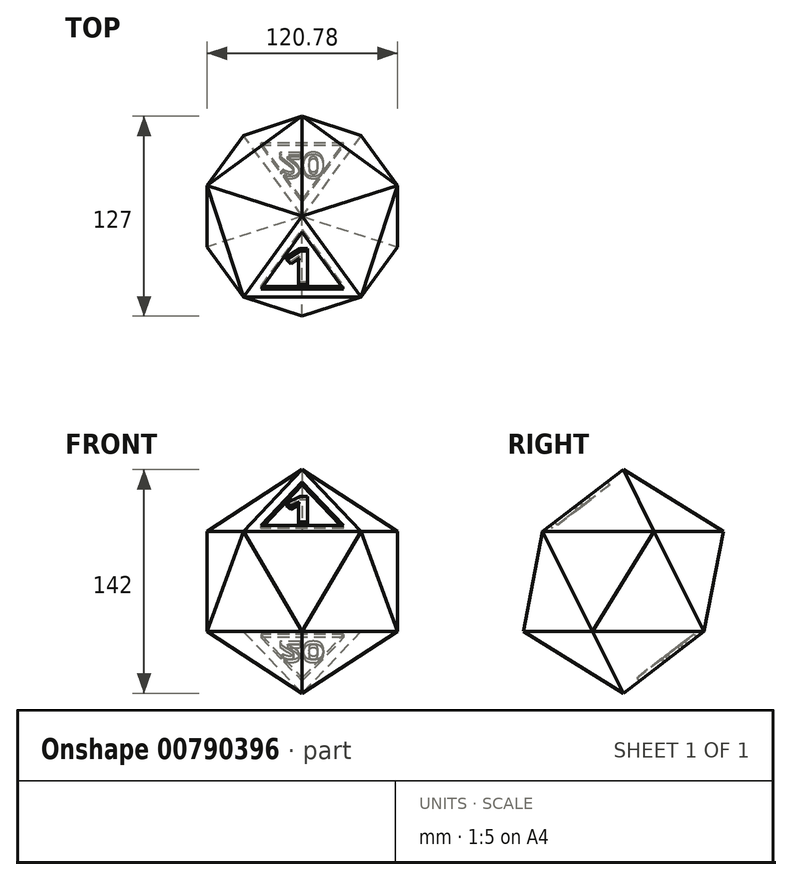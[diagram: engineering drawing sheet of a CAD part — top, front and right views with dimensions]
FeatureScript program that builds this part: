
annotation { "Feature Type Name" : "Feature", "Feature Type Description" : "" }
export const myFeature = defineFeature(function(context is Context, id is Id, definition is map)
    precondition{}
    {
        {
            var Q0;
            Q0=qCreatedBy(makeId("Top.planeOp"),FACE);
            var sketch = newSketch(context, id + "F0", { "sketchPlane" : qUnion([Q0])});
            skCircle(sketch, "E0", {"center": v(37.32, 51.37) * mm, "radius": 74.65 * mm});
            skCircle(sketch, "E1", {"center": v(-37.32, 51.37) * mm, "radius": 74.65 * mm});
            skCircle(sketch, "E2", {"center": v(0, 51.37) * mm, "radius": 64.65 * mm});
            skLineSegment(sketch, "E3", {"start": v(0, 0) * mm, "end": v(39.25, 0) * mm});
            skLineSegment(sketch, "E4", {"start": v(0, 63.5) * mm, "end": v(-63.5, 63.5) * mm});
            skCircle(sketch, "E5", {"center": v(0, 0) * mm, "radius": 63.5 * mm});
            skLineSegment(sketch, "E6", {"start": v(0, 0) * mm, "end": v(0, -63.5) * mm});
            skLineSegment(sketch, "E7", {"start": v(-37.32, 51.37) * mm, "end": v(37.32, 51.37) * mm});
            skLineSegment(sketch, "E8", {"start": v(37.32, 51.37) * mm, "end": v(60.4, -19.62) * mm});
            skLineSegment(sketch, "E9", {"start": v(60.4, -19.62) * mm, "end": v(0, -63.5) * mm});
            skLineSegment(sketch, "E10", {"start": v(0, -63.5) * mm, "end": v(-60.4, -19.62) * mm});
            skLineSegment(sketch, "E11", {"start": v(-60.4, -19.62) * mm, "end": v(-37.32, 51.37) * mm});
            skLineSegment(sketch, "E12", {"start": v(0, 63.5) * mm, "end": v(0, 116.02) * mm});
            skSolve(sketch);
        }
        {
            var Q0;
            Q0=sQuery(id+"F0.wireOp",EDGE,"E4");
            cPlane(context, id + "F1", {"entities" : qUnion([Q0]), "cplaneType" : CPlaneType.LINE_ANGLE, "offset" : 25.4 * mm, "angle" : 180 * degree, "width" : 152.4 * mm, "height" : 152.4 * mm});
        }
        {
            var Q0;
            Q0=qCreatedBy(id+"F1.planeOp",FACE);
            var sketch = newSketch(context, id + "F2", { "sketchPlane" : qUnion([Q0])});
            skLineSegment(sketch, "E13", {"start": v(63.5, 0) * mm, "end": v(0, 0) * mm});
            skLineSegment(sketch, "E14", {"start": v(31.75, 0) * mm, "end": v(63.5, 31.75) * mm});
            skLineSegment(sketch, "E15", {"start": v(31.75, 0) * mm, "end": v(0, -31.75) * mm});
            skLineSegment(sketch, "E16", {"start": v(63.5, 31.75) * mm, "end": v(0, 31.75) * mm});
            skLineSegment(sketch, "E17", {"start": v(0, -31.75) * mm, "end": v(63.5, -31.75) * mm});
            skLineSegment(sketch, "E18", {"start": v(0, 0) * mm, "end": v(0, 31.75) * mm});
            skLineSegment(sketch, "E19", {"start": v(0, 0) * mm, "end": v(0, -31.75) * mm});
            skSolve(sketch);
        }
        {
            var Q0;
            Q0=sQuery(id+"F2.wireOp",EDGE,"E16");
            cPlane(context, id + "F3", {"entities" : qUnion([Q0]), "cplaneType" : CPlaneType.LINE_ANGLE, "offset" : 25.4 * mm, "angle" : 270 * degree, "width" : 152.4 * mm, "height" : 152.4 * mm});
        }
        {
            var Q0;
            Q0=qCreatedBy(id+"F3.planeOp",FACE);
            var sketch = newSketch(context, id + "F4", { "sketchPlane" : qUnion([Q0])});
            skCircle(sketch, "E20.0", {"center": v(0, 0) * mm, "radius": 63.5 * mm});
            skLineSegment(sketch, "E21", {"start": v(-37.32, 51.37) * mm, "end": v(37.32, 51.37) * mm});
            skLineSegment(sketch, "E22", {"start": v(37.32, 51.37) * mm, "end": v(60.4, -19.62) * mm});
            skLineSegment(sketch, "E23", {"start": v(60.4, -19.62) * mm, "end": v(0, -63.5) * mm});
            skLineSegment(sketch, "E24", {"start": v(0, -63.5) * mm, "end": v(-60.4, -19.62) * mm});
            skLineSegment(sketch, "E25", {"start": v(-60.4, -19.62) * mm, "end": v(-37.32, 51.37) * mm});
            skLineSegment(sketch, "E26", {"start": v(0, 51.37) * mm, "end": v(0, 63.5) * mm});
            skLineSegment(sketch, "E27", {"start": v(30.2, -41.56) * mm, "end": v(37.32, -51.37) * mm});
            skLineSegment(sketch, "E28", {"start": v(37.32, -51.37) * mm, "end": v(60.4, -19.62) * mm});
            skLineSegment(sketch, "E29", {"start": v(37.32, -51.37) * mm, "end": v(0, -63.5) * mm});
            skLineSegment(sketch, "E30", {"start": v(-30.2, -41.56) * mm, "end": v(-37.32, -51.37) * mm});
            skLineSegment(sketch, "E31", {"start": v(-37.32, -51.37) * mm, "end": v(0, -63.5) * mm});
            skLineSegment(sketch, "E32", {"start": v(-37.32, -51.37) * mm, "end": v(-60.4, -19.62) * mm});
            skLineSegment(sketch, "E33", {"start": v(-48.86, 15.87) * mm, "end": v(-60.4, 19.62) * mm});
            skLineSegment(sketch, "E34", {"start": v(-60.4, 19.62) * mm, "end": v(-60.4, -19.62) * mm});
            skLineSegment(sketch, "E35", {"start": v(-60.4, 19.62) * mm, "end": v(-37.32, 51.37) * mm});
            skLineSegment(sketch, "E36", {"start": v(-37.32, 51.37) * mm, "end": v(0, 63.5) * mm});
            skLineSegment(sketch, "E37", {"start": v(0, 63.5) * mm, "end": v(37.32, 51.37) * mm});
            skLineSegment(sketch, "E38", {"start": v(60.4, 19.62) * mm, "end": v(37.32, 51.37) * mm});
            skLineSegment(sketch, "E39", {"start": v(60.4, 19.62) * mm, "end": v(60.4, -19.62) * mm});
            skLineSegment(sketch, "E40", {"start": v(48.86, 15.87) * mm, "end": v(60.4, 19.62) * mm});
            skLineSegment(sketch, "E41", {"start": v(0, 0) * mm, "end": v(30.2, -41.56) * mm});
            skLineSegment(sketch, "E42", {"start": v(0, 0) * mm, "end": v(-30.2, -41.56) * mm});
            skLineSegment(sketch, "E43", {"start": v(0, 0) * mm, "end": v(-48.86, 15.87) * mm});
            skLineSegment(sketch, "E44", {"start": v(0, 0) * mm, "end": v(48.86, 15.87) * mm});
            skLineSegment(sketch, "E45", {"start": v(0, 0) * mm, "end": v(0, 51.37) * mm});
            skSolve(sketch);
        }
        {
            var Q0;
            Q0=sQuery(id+"F2.wireOp",EDGE,"E17");
            cPlane(context, id + "F5", {"entities" : qUnion([Q0]), "cplaneType" : CPlaneType.LINE_ANGLE, "offset" : 25.4 * mm, "angle" : 90 * degree, "width" : 152.4 * mm, "height" : 152.4 * mm});
        }
        {
            var Q0;
            Q0=qCreatedBy(id+"F5.planeOp",FACE);
            var sketch = newSketch(context, id + "F6", { "sketchPlane" : qUnion([Q0])});
            skCircle(sketch, "E46.0", {"center": v(0, 0) * mm, "radius": 63.5 * mm});
            skLineSegment(sketch, "E47", {"start": v(-37.32, 51.37) * mm, "end": v(37.32, 51.37) * mm});
            skLineSegment(sketch, "E48", {"start": v(37.32, 51.37) * mm, "end": v(60.4, -19.62) * mm});
            skLineSegment(sketch, "E49", {"start": v(60.4, -19.62) * mm, "end": v(0, -63.5) * mm});
            skLineSegment(sketch, "E50", {"start": v(0, -63.5) * mm, "end": v(-60.4, -19.62) * mm});
            skLineSegment(sketch, "E51", {"start": v(-60.4, -19.62) * mm, "end": v(-37.32, 51.37) * mm});
            skLineSegment(sketch, "E52", {"start": v(0, 51.37) * mm, "end": v(0, 63.5) * mm});
            skLineSegment(sketch, "E53", {"start": v(30.2, -41.56) * mm, "end": v(37.32, -51.37) * mm});
            skLineSegment(sketch, "E54", {"start": v(37.32, -51.37) * mm, "end": v(60.4, -19.62) * mm});
            skLineSegment(sketch, "E55", {"start": v(37.32, -51.37) * mm, "end": v(0, -63.5) * mm});
            skLineSegment(sketch, "E56", {"start": v(-30.2, -41.56) * mm, "end": v(-37.32, -51.37) * mm});
            skLineSegment(sketch, "E57", {"start": v(-37.32, -51.37) * mm, "end": v(0, -63.5) * mm});
            skLineSegment(sketch, "E58", {"start": v(-37.32, -51.37) * mm, "end": v(-60.4, -19.62) * mm});
            skLineSegment(sketch, "E59", {"start": v(-48.86, 15.87) * mm, "end": v(-60.4, 19.62) * mm});
            skLineSegment(sketch, "E60", {"start": v(-60.4, 19.62) * mm, "end": v(-60.4, -19.62) * mm});
            skLineSegment(sketch, "E61", {"start": v(-60.4, 19.62) * mm, "end": v(-37.32, 51.37) * mm});
            skLineSegment(sketch, "E62", {"start": v(-37.32, 51.37) * mm, "end": v(0, 63.5) * mm});
            skLineSegment(sketch, "E63", {"start": v(0, 63.5) * mm, "end": v(37.32, 51.37) * mm});
            skLineSegment(sketch, "E64", {"start": v(60.4, 19.62) * mm, "end": v(37.32, 51.37) * mm});
            skLineSegment(sketch, "E65", {"start": v(60.4, 19.62) * mm, "end": v(60.4, -19.62) * mm});
            skLineSegment(sketch, "E66", {"start": v(48.86, 15.87) * mm, "end": v(60.4, 19.62) * mm});
            skLineSegment(sketch, "E67", {"start": v(0, 0) * mm, "end": v(30.2, -41.56) * mm});
            skLineSegment(sketch, "E68", {"start": v(0, 0) * mm, "end": v(-30.2, -41.56) * mm});
            skLineSegment(sketch, "E69", {"start": v(0, 0) * mm, "end": v(-48.86, 15.88) * mm});
            skLineSegment(sketch, "E70", {"start": v(0, 0) * mm, "end": v(48.86, 15.87) * mm});
            skLineSegment(sketch, "E71", {"start": v(0, 0) * mm, "end": v(0, 51.37) * mm});
            skLineSegment(sketch, "E72.0", {"start": v(-60.4, -19.62) * mm, "end": v(-60.4, 19.62) * mm, "construction": true});
            skLineSegment(sketch, "E73", {"start": v(63.5, 0) * mm, "end": v(74.27, 0) * mm});
            skPoint(sketch, "E73.startSnap0", {"position": v(60.4, 0) * mm});
            skSolve(sketch);
        }
        {
            var Q0;
            Q0=qCreatedBy(makeId("Front.planeOp"),FACE);
            var sketch = newSketch(context, id + "F7", { "sketchPlane" : qUnion([Q0])});
            skLineSegment(sketch, "E74", {"start": v(39.25, 31.75) * mm, "end": v(0, 31.75) * mm});
            skLineSegment(sketch, "E75", {"start": v(39.25, 31.75) * mm, "end": v(0, 71) * mm});
            skLineSegment(sketch, "E76", {"start": v(0, -31.75) * mm, "end": v(39.25, -31.75) * mm});
            skLineSegment(sketch, "E77", {"start": v(39.25, -31.75) * mm, "end": v(0, -71) * mm});
            skLineSegment(sketch, "E78", {"start": v(39.25, -31.75) * mm, "end": v(63.5, -31.75) * mm});
            skLineSegment(sketch, "E79", {"start": v(63.5, -31.75) * mm, "end": v(0, 0) * mm});
            skCircle(sketch, "E80", {"center": v(0, 0) * mm, "radius": 71 * mm});
            skLineSegment(sketch, "E81", {"start": v(0, 0) * mm, "end": v(0, -71) * mm});
            skLineSegment(sketch, "E82", {"start": v(0, 0) * mm, "end": v(0, 71) * mm});
            skLineSegment(sketch, "E83", {"start": v(39.25, 31.75) * mm, "end": v(71, 0) * mm});
            skLineSegment(sketch, "E84", {"start": v(0, 0) * mm, "end": v(39.25, 0) * mm});
            skLineSegment(sketch, "E85", {"start": v(39.25, 0) * mm, "end": v(39.25, 31.75) * mm});
            skSolve(sketch);
        }
        {
            var Q0;
            Q0=qCreatedBy(makeId("Top.planeOp"),FACE);
            var sketch = newSketch(context, id + "F8", { "sketchPlane" : qUnion([Q0])});
            skLineSegment(sketch, "E86", {"start": v(0, 0) * mm, "end": v(71, 0) * mm});
            skCircle(sketch, "E87", {"center": v(0, 0) * mm, "radius": 71 * mm});
            skLineSegment(sketch, "E88", {"start": v(0, 0) * mm, "end": v(67.52, -21.94) * mm});
            skLineSegment(sketch, "E89", {"start": v(0, 0) * mm, "end": v(67.52, 21.94) * mm});
            skLineSegment(sketch, "E90", {"start": v(0, 0) * mm, "end": v(41.73, 57.44) * mm});
            skLineSegment(sketch, "E91", {"start": v(0, 0) * mm, "end": v(0, 71) * mm});
            skLineSegment(sketch, "E92", {"start": v(0, 0) * mm, "end": v(41.73, -57.44) * mm});
            skLineSegment(sketch, "E93", {"start": v(0, 0) * mm, "end": v(0, -71) * mm});
            skLineSegment(sketch, "E94", {"start": v(0, 0) * mm, "end": v(-41.73, -57.44) * mm});
            skLineSegment(sketch, "E95", {"start": v(0, 0) * mm, "end": v(-41.73, 57.44) * mm});
            skLineSegment(sketch, "E96", {"start": v(0, 0) * mm, "end": v(-67.52, 21.94) * mm});
            skLineSegment(sketch, "E97", {"start": v(0, 0) * mm, "end": v(-67.52, -21.94) * mm});
            skSolve(sketch);
        }
        {
            var Q0;
            {var subQ0=sQuery(id+"F7.wireOp",EDGE,"E81");var subQ1=makeQuery(id+"F7.imprint","INTERSECT",VERTEX,{"derivedFrom":[sQuery(id+"F7.wireOp",EDGE,"E76"),subQ0]});Q0=makeQuery(id+"F7.imprint","IMPRINT",FACE,{"disambiguationData":[TD([[makeQuery(id+"F7.imprint","IMPRINT",EDGE,{"disambiguationData":[TD([[subQ1,1.0]])],"derivedFrom":subQ0}),-1.0]])]});}
            var Q1;
            Q1=sQuery(id+"F7.wireOp",EDGE,"E81");
            revolve(context, id + "F9", {"surfaceOperationType" : NewSurfaceOperationType.NEW, "entities" : qUnion([Q0]), "axis" : qUnion([Q1]), "revolveType" : RevolveType.FULL});
        }
        {
            var Q0;
            Q0=sQuery(id+"F6.wireOp",VERTEX,"E53.end");
            var Q1;
            Q1=sQuery(id+"F6.wireOp",VERTEX,"E67.start");
            var Q2;
            Q2=sQuery(id+"F7.wireOp",VERTEX,"E77.end");
            cPlane(context, id + "F10", {"entities" : qUnion([Q0, Q1, Q2]), "cplaneType" : CPlaneType.THREE_POINT, "offset" : 25.4 * mm, "width" : 152.4 * mm, "height" : 152.4 * mm});
        }
        {
            var Q0;
            Q0=qCreatedBy(id+"F10.planeOp",FACE);
            var sketch = newSketch(context, id + "F11", { "sketchPlane" : qUnion([Q0])});
            skLineSegment(sketch, "E98", {"start": v(0, -71) * mm, "end": v(-51.37, -31.75) * mm});
            skLineSegment(sketch, "E99", {"start": v(-51.37, -31.75) * mm, "end": v(-63.5, -31.75) * mm});
            skLineSegment(sketch, "E100", {"start": v(-63.5, -31.75) * mm, "end": v(-63.5, -71) * mm});
            skLineSegment(sketch, "E101", {"start": v(-63.5, -71) * mm, "end": v(0, -71) * mm});
            skSolve(sketch);
        }
        {
            var Q0;
            {var subQ0=sQuery(id+"F11.wireOp",EDGE,"E98");Q0=makeQuery(id+"F11.imprint","IMPRINT",FACE,{"disambiguationData":[TD([[makeQuery(id+"F11.imprint","IMPRINT",EDGE,{"derivedFrom":subQ0}),1.0]])]});}
            var Q1;
            Q1=sQuery(id+"F6.wireOp",VERTEX,"E48.end");
            var Q2;
            Q2=sQuery(id+"F6.wireOp",VERTEX,"E49.end");
            extrude(context, id + "F12", {"entities" : qUnion([Q0]), "operationType" : NewBodyOperationType.REMOVE, "endBound" : BoundingType.UP_TO_VERTEX, "depth" : 25.4 * mm, "endBoundEntityVertex" : qUnion([Q1]), "offsetDistance" : 25.4 * mm, "hasSecondDirection" : true, "secondDirectionBound" : SecondDirectionBoundingType.UP_TO_VERTEX, "secondDirectionOppositeDirection" : true, "secondDirectionDepth" : 25.4 * mm, "secondDirectionBoundEntityVertex" : qUnion([Q2])});
        }
        {
            var Q0;
            Q0=sQuery(id+"F7.wireOp",VERTEX,"E77.end");
            var Q1;
            Q1=sQuery(id+"F6.wireOp",VERTEX,"E67.start");
            var Q2;
            Q2=sQuery(id+"F6.wireOp",VERTEX,"E56.end");
            cPlane(context, id + "F13", {"entities" : qUnion([Q0, Q1, Q2]), "cplaneType" : CPlaneType.THREE_POINT, "offset" : 25.4 * mm, "width" : 152.4 * mm, "height" : 152.4 * mm});
        }
        {
            var Q0;
            Q0=qCreatedBy(id+"F13.planeOp",FACE);
            var sketch = newSketch(context, id + "F14", { "sketchPlane" : qUnion([Q0])});
            skLineSegment(sketch, "E102", {"start": v(0, -71) * mm, "end": v(51.37, -31.75) * mm});
            skLineSegment(sketch, "E103", {"start": v(0, -71) * mm, "end": v(63.5, -71) * mm});
            skLineSegment(sketch, "E104", {"start": v(63.5, -71) * mm, "end": v(63.5, -31.75) * mm});
            skLineSegment(sketch, "E105", {"start": v(63.5, -31.75) * mm, "end": v(51.37, -31.75) * mm});
            skSolve(sketch);
        }
        {
            var Q0;
            {var subQ0=sQuery(id+"F14.wireOp",EDGE,"E102");Q0=makeQuery(id+"F14.imprint","IMPRINT",FACE,{"disambiguationData":[TD([[makeQuery(id+"F14.imprint","IMPRINT",EDGE,{"derivedFrom":subQ0}),-1.0]])]});}
            var Q1;
            Q1=sQuery(id+"F6.wireOp",VERTEX,"E49.end");
            var Q2;
            Q2=sQuery(id+"F6.wireOp",VERTEX,"E50.end");
            extrude(context, id + "F15", {"entities" : qUnion([Q0]), "operationType" : NewBodyOperationType.REMOVE, "endBound" : BoundingType.UP_TO_VERTEX, "oppositeDirection" : true, "depth" : 25.4 * mm, "endBoundEntityVertex" : qUnion([Q1]), "offsetDistance" : 25.4 * mm, "hasSecondDirection" : true, "secondDirectionBound" : SecondDirectionBoundingType.UP_TO_VERTEX, "secondDirectionOppositeDirection" : false, "secondDirectionDepth" : 25.4 * mm, "secondDirectionBoundEntityVertex" : qUnion([Q2])});
        }
        {
            var Q0;
            Q0=sQuery(id+"F6.wireOp",VERTEX,"E67.start");
            var Q1;
            Q1=sQuery(id+"F7.wireOp",VERTEX,"E77.end");
            var Q2;
            Q2=sQuery(id+"F6.wireOp",VERTEX,"E59.end");
            cPlane(context, id + "F16", {"entities" : qUnion([Q0, Q1, Q2]), "cplaneType" : CPlaneType.THREE_POINT, "offset" : 25.4 * mm, "width" : 152.4 * mm, "height" : 152.4 * mm});
        }
        {
            var Q0;
            Q0=qCreatedBy(id+"F16.planeOp",FACE);
            var sketch = newSketch(context, id + "F17", { "sketchPlane" : qUnion([Q0])});
            skLineSegment(sketch, "E106", {"start": v(0, -71) * mm, "end": v(-51.37, -31.75) * mm});
            skLineSegment(sketch, "E107", {"start": v(0, -71) * mm, "end": v(-63.5, -71) * mm});
            skLineSegment(sketch, "E108", {"start": v(-63.5, -71) * mm, "end": v(-63.5, -31.75) * mm});
            skLineSegment(sketch, "E109", {"start": v(-63.5, -31.75) * mm, "end": v(-51.37, -31.75) * mm});
            skSolve(sketch);
        }
        {
            var Q0;
            {var subQ0=sQuery(id+"F17.wireOp",EDGE,"E106");Q0=makeQuery(id+"F17.imprint","IMPRINT",FACE,{"disambiguationData":[TD([[makeQuery(id+"F17.imprint","IMPRINT",EDGE,{"derivedFrom":subQ0}),1.0]])]});}
            var Q1;
            Q1=sQuery(id+"F6.wireOp",VERTEX,"E47.start");
            var Q2;
            Q2=sQuery(id+"F6.wireOp",VERTEX,"E50.end");
            extrude(context, id + "F18", {"entities" : qUnion([Q0]), "operationType" : NewBodyOperationType.REMOVE, "endBound" : BoundingType.UP_TO_VERTEX, "oppositeDirection" : true, "depth" : 25.4 * mm, "endBoundEntityVertex" : qUnion([Q1]), "offsetDistance" : 25.4 * mm, "hasSecondDirection" : true, "secondDirectionBound" : SecondDirectionBoundingType.UP_TO_VERTEX, "secondDirectionOppositeDirection" : false, "secondDirectionDepth" : 25.4 * mm, "secondDirectionBoundEntityVertex" : qUnion([Q2])});
        }
        {
            var Q0;
            Q0=sQuery(id+"F7.wireOp",VERTEX,"E77.end");
            var Q1;
            Q1=sQuery(id+"F6.wireOp",VERTEX,"E67.start");
            var Q2;
            Q2=sQuery(id+"F6.wireOp",VERTEX,"E52.end");
            cPlane(context, id + "F19", {"entities" : qUnion([Q0, Q1, Q2]), "cplaneType" : CPlaneType.THREE_POINT, "offset" : 25.4 * mm, "width" : 152.4 * mm, "height" : 152.4 * mm});
        }
        {
            var Q0;
            Q0=qCreatedBy(id+"F19.planeOp",FACE);
            var sketch = newSketch(context, id + "F20", { "sketchPlane" : qUnion([Q0])});
            skLineSegment(sketch, "E110", {"start": v(0, -71) * mm, "end": v(51.37, -31.75) * mm});
            skLineSegment(sketch, "E111", {"start": v(0, -71) * mm, "end": v(63.5, -71) * mm});
            skLineSegment(sketch, "E112", {"start": v(63.5, -71) * mm, "end": v(63.5, -31.75) * mm});
            skLineSegment(sketch, "E113", {"start": v(63.5, -31.75) * mm, "end": v(51.37, -31.75) * mm});
            skSolve(sketch);
        }
        {
            var Q0;
            {var subQ0=sQuery(id+"F20.wireOp",EDGE,"E110");Q0=makeQuery(id+"F20.imprint","IMPRINT",FACE,{"disambiguationData":[TD([[makeQuery(id+"F20.imprint","IMPRINT",EDGE,{"derivedFrom":subQ0}),-1.0]])]});}
            var Q1;
            Q1=sQuery(id+"F6.wireOp",VERTEX,"E47.start");
            var Q2;
            Q2=sQuery(id+"F6.wireOp",VERTEX,"E47.end");
            extrude(context, id + "F21", {"entities" : qUnion([Q0]), "operationType" : NewBodyOperationType.REMOVE, "endBound" : BoundingType.UP_TO_VERTEX, "oppositeDirection" : true, "depth" : 25.4 * mm, "endBoundEntityVertex" : qUnion([Q1]), "offsetDistance" : 25.4 * mm, "hasSecondDirection" : true, "secondDirectionBound" : SecondDirectionBoundingType.UP_TO_VERTEX, "secondDirectionOppositeDirection" : false, "secondDirectionDepth" : 25.4 * mm, "secondDirectionBoundEntityVertex" : qUnion([Q2])});
        }
        {
            var Q0;
            Q0=sQuery(id+"F6.wireOp",VERTEX,"E64.start");
            var Q1;
            Q1=sQuery(id+"F6.wireOp",VERTEX,"E67.start");
            var Q2;
            Q2=sQuery(id+"F7.wireOp",VERTEX,"E77.end");
            cPlane(context, id + "F22", {"entities" : qUnion([Q0, Q1, Q2]), "cplaneType" : CPlaneType.THREE_POINT, "offset" : 25.4 * mm, "width" : 152.4 * mm, "height" : 152.4 * mm});
        }
        {
            var Q0;
            Q0=qCreatedBy(id+"F22.planeOp",FACE);
            var sketch = newSketch(context, id + "F23", { "sketchPlane" : qUnion([Q0])});
            skLineSegment(sketch, "E114", {"start": v(0, -71) * mm, "end": v(-51.37, -31.75) * mm});
            skLineSegment(sketch, "E115", {"start": v(-51.37, -31.75) * mm, "end": v(-63.5, -31.75) * mm});
            skLineSegment(sketch, "E116", {"start": v(-63.5, -31.75) * mm, "end": v(-63.5, -71) * mm});
            skLineSegment(sketch, "E117", {"start": v(-63.5, -71) * mm, "end": v(0, -71) * mm});
            skSolve(sketch);
        }
        {
            var Q0;
            {var subQ0=sQuery(id+"F23.wireOp",EDGE,"E114");Q0=makeQuery(id+"F23.imprint","IMPRINT",FACE,{"disambiguationData":[TD([[makeQuery(id+"F23.imprint","IMPRINT",EDGE,{"derivedFrom":subQ0}),1.0]])]});}
            var Q1;
            Q1=sQuery(id+"F6.wireOp",VERTEX,"E47.end");
            var Q2;
            Q2=sQuery(id+"F6.wireOp",VERTEX,"E48.end");
            extrude(context, id + "F24", {"entities" : qUnion([Q0]), "operationType" : NewBodyOperationType.REMOVE, "endBound" : BoundingType.UP_TO_VERTEX, "depth" : 25.4 * mm, "endBoundEntityVertex" : qUnion([Q1]), "offsetDistance" : 25.4 * mm, "hasSecondDirection" : true, "secondDirectionBound" : SecondDirectionBoundingType.UP_TO_VERTEX, "secondDirectionOppositeDirection" : true, "secondDirectionDepth" : 25.4 * mm, "secondDirectionBoundEntityVertex" : qUnion([Q2])});
        }
        {
            var Q0;
            Q0=sQuery(id+"F6.wireOp",EDGE,"E49");
            cPoint(context, id + "F25", {"entities" : qUnion([Q0]), "parameter" : 0.5});
        }
        {
            var Q0;
            Q0=qCreatedBy(id+"F25",VERTEX);
            var Q1;
            Q1=sQuery(id+"F6.wireOp",VERTEX,"E53.end");
            var Q2;
            Q2=sQuery(id+"F4.wireOp",VERTEX,"E21.end");
            cPlane(context, id + "F26", {"entities" : qUnion([Q0, Q1, Q2]), "cplaneType" : CPlaneType.THREE_POINT, "offset" : 25.4 * mm, "width" : 152.4 * mm, "height" : 152.4 * mm});
        }
        {
            var Q0;
            Q0=qCreatedBy(id+"F26.planeOp",FACE);
            var sketch = newSketch(context, id + "F27", { "sketchPlane" : qUnion([Q0])});
            skLineSegment(sketch, "E118.bottom", {"start": v(-51.37, -31.75) * mm, "end": v(-71, -31.75) * mm});
            skLineSegment(sketch, "E118.top", {"start": v(-51.37, 31.75) * mm, "end": v(-71, 31.75) * mm});
            skLineSegment(sketch, "E118.left", {"start": v(-51.37, -31.75) * mm, "end": v(-51.37, 31.75) * mm});
            skLineSegment(sketch, "E118.right", {"start": v(-71, -31.75) * mm, "end": v(-71, 31.75) * mm});
            skLineSegment(sketch, "E119", {"start": v(-51.37, -31.75) * mm, "end": v(-63.5, 31.75) * mm});
            skSolve(sketch);
        }
        {
            var Q0;
            Q0=makeQuery(id+"F27.imprint","IMPRINT",FACE,{"disambiguationData":[TD([[makeQuery(id+"F27.imprint","IMPRINT",EDGE,{"derivedFrom":sQuery(id+"F27.wireOp",EDGE,"E118.bottom")}),-1.0]])]});
            var Q1;
            Q1=sQuery(id+"F6.wireOp",VERTEX,"E48.end");
            var Q2;
            Q2=sQuery(id+"F6.wireOp",VERTEX,"E49.end");
            extrude(context, id + "F28", {"entities" : qUnion([Q0]), "operationType" : NewBodyOperationType.REMOVE, "endBound" : BoundingType.THROUGH_ALL, "depth" : 25.4 * mm, "endBoundEntityVertex" : qUnion([Q1]), "offsetDistance" : 25.4 * mm, "hasSecondDirection" : true, "secondDirectionBound" : SecondDirectionBoundingType.THROUGH_ALL, "secondDirectionOppositeDirection" : true, "secondDirectionDepth" : 25.4 * mm, "secondDirectionBoundEntityVertex" : qUnion([Q2])});
        }
        {
            var Q0;
            Q0=sQuery(id+"F4.wireOp",EDGE,"E22");
            cPoint(context, id + "F29", {"entities" : qUnion([Q0]), "parameter" : 0.5});
        }
        {
            var Q0;
            Q0=sQuery(id+"F6.wireOp",VERTEX,"E48.end");
            var Q1;
            Q1=qCreatedBy(id+"F29",VERTEX);
            var Q2;
            Q2=sQuery(id+"F4.wireOp",VERTEX,"E38.start");
            cPlane(context, id + "F30", {"entities" : qUnion([Q0, Q1, Q2]), "cplaneType" : CPlaneType.THREE_POINT, "offset" : 25.4 * mm, "width" : 152.4 * mm, "height" : 152.4 * mm});
        }
        {
            var Q0;
            Q0=qCreatedBy(id+"F30.planeOp",FACE);
            var sketch = newSketch(context, id + "F31", { "sketchPlane" : qUnion([Q0])});
            skLineSegment(sketch, "E120.bottom", {"start": v(51.37, 31.75) * mm, "end": v(71, 31.75) * mm});
            skLineSegment(sketch, "E120.top", {"start": v(51.37, -31.75) * mm, "end": v(71, -31.75) * mm});
            skLineSegment(sketch, "E120.left", {"start": v(51.37, 31.75) * mm, "end": v(51.37, -31.75) * mm});
            skLineSegment(sketch, "E120.right", {"start": v(71, 31.75) * mm, "end": v(71, -31.75) * mm});
            skLineSegment(sketch, "E121", {"start": v(51.37, 31.75) * mm, "end": v(63.5, -31.75) * mm});
            skSolve(sketch);
        }
        {
            var Q0;
            Q0=makeQuery(id+"F58.imprint","IMPRINT",FACE,{"disambiguationData":[TD([[makeQuery(id+"F58.imprint","IMPRINT",EDGE,{"derivedFrom":sQuery(id+"F58.wireOp",EDGE,"E136.bottom")}),-1.0]])]});
            var Q1;
            Q1=makeQuery(id+"F31.imprint","IMPRINT",FACE,{"disambiguationData":[TD([[makeQuery(id+"F31.imprint","IMPRINT",EDGE,{"derivedFrom":sQuery(id+"F31.wireOp",EDGE,"E120.bottom")}),-1.0]])]});
            extrude(context, id + "F32", {"entities" : qUnion([Q0, Q1]), "operationType" : NewBodyOperationType.REMOVE, "endBound" : BoundingType.THROUGH_ALL, "oppositeDirection" : true, "depth" : 25.4 * mm, "offsetDistance" : 25.4 * mm, "hasSecondDirection" : true, "secondDirectionBound" : SecondDirectionBoundingType.THROUGH_ALL, "secondDirectionOppositeDirection" : false, "secondDirectionDepth" : 25.4 * mm});
        }
        {
            var Q0;
            Q0=sQuery(id+"F6.wireOp",VERTEX,"E64.start");
            var Q1;
            Q1=sQuery(id+"F6.wireOp",VERTEX,"E66.start");
            var Q2;
            Q2=sQuery(id+"F4.wireOp",VERTEX,"E22.end");
            cPlane(context, id + "F33", {"entities" : qUnion([Q0, Q1, Q2]), "cplaneType" : CPlaneType.THREE_POINT, "offset" : 25.4 * mm, "width" : 152.4 * mm, "height" : 152.4 * mm});
        }
        {
            var Q0;
            Q0=qCreatedBy(id+"F33.planeOp",FACE);
            var sketch = newSketch(context, id + "F34", { "sketchPlane" : qUnion([Q0])});
            skLineSegment(sketch, "E122.bottom", {"start": v(51.37, -31.75) * mm, "end": v(71, -31.75) * mm});
            skLineSegment(sketch, "E122.top", {"start": v(51.37, 31.75) * mm, "end": v(71, 31.75) * mm});
            skLineSegment(sketch, "E122.left", {"start": v(51.37, -31.75) * mm, "end": v(51.37, 31.75) * mm});
            skLineSegment(sketch, "E122.right", {"start": v(71, -31.75) * mm, "end": v(71, 31.75) * mm});
            skLineSegment(sketch, "E123", {"start": v(51.37, -31.75) * mm, "end": v(63.5, 31.75) * mm});
            skSolve(sketch);
        }
        {
            var Q0;
            Q0=makeQuery(id+"F55.imprint","IMPRINT",FACE,{"disambiguationData":[TD([[makeQuery(id+"F55.imprint","IMPRINT",EDGE,{"derivedFrom":sQuery(id+"F55.wireOp",EDGE,"E134.bottom")}),-1.0]])]});
            var Q1;
            Q1=makeQuery(id+"F34.imprint","IMPRINT",FACE,{"disambiguationData":[TD([[makeQuery(id+"F34.imprint","IMPRINT",EDGE,{"derivedFrom":sQuery(id+"F34.wireOp",EDGE,"E122.bottom")}),1.0]])]});
            extrude(context, id + "F35", {"entities" : qUnion([Q0, Q1]), "operationType" : NewBodyOperationType.REMOVE, "endBound" : BoundingType.THROUGH_ALL, "oppositeDirection" : true, "depth" : 25.4 * mm, "offsetDistance" : 25.4 * mm, "hasSecondDirection" : true, "secondDirectionBound" : SecondDirectionBoundingType.THROUGH_ALL, "secondDirectionOppositeDirection" : false, "secondDirectionDepth" : 25.4 * mm});
        }
        {
            var Q0;
            Q0=sQuery(id+"F4.wireOp",EDGE,"E23");
            cPoint(context, id + "F36", {"entities" : qUnion([Q0]), "parameter" : 0.5});
        }
        {
            var Q0;
            Q0=qCreatedBy(id+"F36",VERTEX);
            var Q1;
            Q1=sQuery(id+"F4.wireOp",VERTEX,"E27.end");
            var Q2;
            Q2=sQuery(id+"F6.wireOp",VERTEX,"E47.end");
            cPlane(context, id + "F37", {"entities" : qUnion([Q0, Q1, Q2]), "cplaneType" : CPlaneType.THREE_POINT, "offset" : 25.4 * mm, "width" : 152.4 * mm, "height" : 152.4 * mm});
        }
        {
            var Q0;
            Q0=qCreatedBy(id+"F37.planeOp",FACE);
            var sketch = newSketch(context, id + "F38", { "sketchPlane" : qUnion([Q0])});
            skLineSegment(sketch, "E124.bottom", {"start": v(51.37, 31.75) * mm, "end": v(71, 31.75) * mm});
            skLineSegment(sketch, "E124.top", {"start": v(51.37, -31.75) * mm, "end": v(71, -31.75) * mm});
            skLineSegment(sketch, "E124.left", {"start": v(51.37, 31.75) * mm, "end": v(51.37, -31.75) * mm});
            skLineSegment(sketch, "E124.right", {"start": v(71, 31.75) * mm, "end": v(71, -31.75) * mm});
            skLineSegment(sketch, "E125", {"start": v(51.37, 31.75) * mm, "end": v(63.5, -31.75) * mm});
            skSolve(sketch);
        }
        {
            var Q0;
            Q0=makeQuery(id+"F38.imprint","IMPRINT",FACE,{"disambiguationData":[TD([[makeQuery(id+"F38.imprint","IMPRINT",EDGE,{"derivedFrom":sQuery(id+"F38.wireOp",EDGE,"E124.bottom")}),-1.0]])]});
            extrude(context, id + "F39", {"entities" : qUnion([Q0]), "operationType" : NewBodyOperationType.REMOVE, "endBound" : BoundingType.THROUGH_ALL, "oppositeDirection" : true, "depth" : 25.4 * mm, "offsetDistance" : 25.4 * mm, "hasSecondDirection" : true, "secondDirectionBound" : SecondDirectionBoundingType.THROUGH_ALL, "secondDirectionOppositeDirection" : false, "secondDirectionDepth" : 25.4 * mm});
        }
        {
            var Q0;
            Q0=sQuery(id+"F6.wireOp",VERTEX,"E52.start");
            var Q1;
            Q1=sQuery(id+"F6.wireOp",VERTEX,"E52.end");
            var Q2;
            Q2=sQuery(id+"F4.wireOp",VERTEX,"E23.end");
            cPlane(context, id + "F40", {"entities" : qUnion([Q0, Q1, Q2]), "cplaneType" : CPlaneType.THREE_POINT, "offset" : 25.4 * mm, "width" : 152.4 * mm, "height" : 152.4 * mm});
        }
        {
            var Q0;
            Q0=qCreatedBy(id+"F40.planeOp",FACE);
            var sketch = newSketch(context, id + "F41", { "sketchPlane" : qUnion([Q0])});
            skLineSegment(sketch, "E126.bottom", {"start": v(-51.37, -31.75) * mm, "end": v(-71, -31.75) * mm});
            skLineSegment(sketch, "E126.top", {"start": v(-51.37, 31.75) * mm, "end": v(-71, 31.75) * mm});
            skLineSegment(sketch, "E126.left", {"start": v(-51.37, -31.75) * mm, "end": v(-51.37, 31.75) * mm});
            skLineSegment(sketch, "E126.right", {"start": v(-71, -31.75) * mm, "end": v(-71, 31.75) * mm});
            skLineSegment(sketch, "E127", {"start": v(-51.37, -31.75) * mm, "end": v(-63.5, 31.75) * mm});
            skSolve(sketch);
        }
        {
            var Q0;
            Q0=makeQuery(id+"F41.imprint","IMPRINT",FACE,{"disambiguationData":[TD([[makeQuery(id+"F41.imprint","IMPRINT",EDGE,{"derivedFrom":sQuery(id+"F41.wireOp",EDGE,"E126.bottom")}),-1.0]])]});
            extrude(context, id + "F42", {"entities" : qUnion([Q0]), "operationType" : NewBodyOperationType.REMOVE, "endBound" : BoundingType.THROUGH_ALL, "oppositeDirection" : true, "depth" : 25.4 * mm, "offsetDistance" : 25.4 * mm, "hasSecondDirection" : true, "secondDirectionBound" : SecondDirectionBoundingType.THROUGH_ALL, "secondDirectionOppositeDirection" : false, "secondDirectionDepth" : 25.4 * mm});
        }
        {
            var Q0;
            Q0=sQuery(id+"F4.wireOp",VERTEX,"E30.end");
            var Q1;
            Q1=sQuery(id+"F4.wireOp",VERTEX,"E30.start");
            var Q2;
            Q2=sQuery(id+"F6.wireOp",VERTEX,"E47.start");
            cPlane(context, id + "F43", {"entities" : qUnion([Q0, Q1, Q2]), "cplaneType" : CPlaneType.THREE_POINT, "offset" : 25.4 * mm, "width" : 152.4 * mm, "height" : 152.4 * mm});
        }
        {
            var Q0;
            Q0=qCreatedBy(id+"F43.planeOp",FACE);
            var sketch = newSketch(context, id + "F44", { "sketchPlane" : qUnion([Q0])});
            skLineSegment(sketch, "E128.bottom", {"start": v(-51.37, 31.75) * mm, "end": v(-71, 31.75) * mm});
            skLineSegment(sketch, "E128.top", {"start": v(-51.37, -31.75) * mm, "end": v(-71, -31.75) * mm});
            skLineSegment(sketch, "E128.left", {"start": v(-51.37, 31.75) * mm, "end": v(-51.37, -31.75) * mm});
            skLineSegment(sketch, "E128.right", {"start": v(-71, 31.75) * mm, "end": v(-71, -31.75) * mm});
            skLineSegment(sketch, "E129", {"start": v(-51.37, 31.75) * mm, "end": v(-63.5, -31.75) * mm});
            skSolve(sketch);
        }
        {
            var Q0;
            Q0=makeQuery(id+"F44.imprint","IMPRINT",FACE,{"disambiguationData":[TD([[makeQuery(id+"F44.imprint","IMPRINT",EDGE,{"derivedFrom":sQuery(id+"F44.wireOp",EDGE,"E128.bottom")}),1.0]])]});
            extrude(context, id + "F45", {"entities" : qUnion([Q0]), "operationType" : NewBodyOperationType.REMOVE, "endBound" : BoundingType.THROUGH_ALL, "oppositeDirection" : true, "depth" : 25.4 * mm, "offsetDistance" : 25.4 * mm, "hasSecondDirection" : true, "secondDirectionBound" : SecondDirectionBoundingType.THROUGH_ALL, "secondDirectionOppositeDirection" : false, "secondDirectionDepth" : 25.4 * mm});
        }
        {
            var Q0;
            Q0=sQuery(id+"F6.wireOp",VERTEX,"E59.start");
            var Q1;
            Q1=sQuery(id+"F6.wireOp",VERTEX,"E59.end");
            var Q2;
            Q2=sQuery(id+"F4.wireOp",VERTEX,"E24.end");
            cPlane(context, id + "F46", {"entities" : qUnion([Q0, Q1, Q2]), "cplaneType" : CPlaneType.THREE_POINT, "offset" : 25.4 * mm, "width" : 152.4 * mm, "height" : 152.4 * mm});
        }
        {
            var Q0;
            Q0=qCreatedBy(id+"F46.planeOp",FACE);
            var sketch = newSketch(context, id + "F47", { "sketchPlane" : qUnion([Q0])});
            skLineSegment(sketch, "E130.bottom", {"start": v(-51.37, -31.75) * mm, "end": v(-71, -31.75) * mm});
            skLineSegment(sketch, "E130.top", {"start": v(-51.37, 31.75) * mm, "end": v(-71, 31.75) * mm});
            skLineSegment(sketch, "E130.left", {"start": v(-51.37, -31.75) * mm, "end": v(-51.37, 31.75) * mm});
            skLineSegment(sketch, "E130.right", {"start": v(-71, -31.75) * mm, "end": v(-71, 31.75) * mm});
            skLineSegment(sketch, "E131", {"start": v(-51.37, -31.75) * mm, "end": v(-63.5, 31.75) * mm});
            skSolve(sketch);
        }
        {
            var Q0;
            Q0=makeQuery(id+"F47.imprint","IMPRINT",FACE,{"disambiguationData":[TD([[makeQuery(id+"F47.imprint","IMPRINT",EDGE,{"derivedFrom":sQuery(id+"F47.wireOp",EDGE,"E130.bottom")}),-1.0]])]});
            extrude(context, id + "F48", {"entities" : qUnion([Q0]), "operationType" : NewBodyOperationType.REMOVE, "endBound" : BoundingType.THROUGH_ALL, "oppositeDirection" : true, "depth" : 25.4 * mm, "offsetDistance" : 25.4 * mm, "hasSecondDirection" : true, "secondDirectionBound" : SecondDirectionBoundingType.THROUGH_ALL, "secondDirectionOppositeDirection" : false, "secondDirectionDepth" : 25.4 * mm});
        }
        {
            var Q0;
            Q0=sQuery(id+"F4.wireOp",EDGE,"E25");
            cPoint(context, id + "F49", {"entities" : qUnion([Q0]), "parameter" : 0.5});
        }
        {
            var Q0;
            Q0=sQuery(id+"F6.wireOp",VERTEX,"E50.end");
            var Q1;
            Q1=qCreatedBy(id+"F49",VERTEX);
            var Q2;
            Q2=sQuery(id+"F4.wireOp",VERTEX,"E33.end");
            cPlane(context, id + "F50", {"entities" : qUnion([Q0, Q1, Q2]), "cplaneType" : CPlaneType.THREE_POINT, "offset" : 25.4 * mm, "width" : 152.4 * mm, "height" : 152.4 * mm});
        }
        {
            var Q0;
            Q0=qCreatedBy(id+"F50.planeOp",FACE);
            var sketch = newSketch(context, id + "F51", { "sketchPlane" : qUnion([Q0])});
            skLineSegment(sketch, "E132.bottom", {"start": v(51.37, 31.75) * mm, "end": v(71, 31.75) * mm});
            skLineSegment(sketch, "E132.top", {"start": v(51.37, -31.75) * mm, "end": v(71, -31.75) * mm});
            skLineSegment(sketch, "E132.left", {"start": v(51.37, 31.75) * mm, "end": v(51.37, -31.75) * mm});
            skLineSegment(sketch, "E132.right", {"start": v(71, 31.75) * mm, "end": v(71, -31.75) * mm});
            skLineSegment(sketch, "E133", {"start": v(51.37, 31.75) * mm, "end": v(63.5, -31.75) * mm});
            skSolve(sketch);
        }
        {
            var Q0;
            Q0=makeQuery(id+"F51.imprint","IMPRINT",FACE,{"disambiguationData":[TD([[makeQuery(id+"F51.imprint","IMPRINT",EDGE,{"derivedFrom":sQuery(id+"F51.wireOp",EDGE,"E132.bottom")}),-1.0]])]});
            extrude(context, id + "F52", {"entities" : qUnion([Q0]), "operationType" : NewBodyOperationType.REMOVE, "endBound" : BoundingType.THROUGH_ALL, "oppositeDirection" : true, "depth" : 25.4 * mm, "offsetDistance" : 25.4 * mm, "hasSecondDirection" : true, "secondDirectionBound" : SecondDirectionBoundingType.THROUGH_ALL, "secondDirectionOppositeDirection" : false, "secondDirectionDepth" : 25.4 * mm});
        }
        {
            var Q0;
            Q0=sQuery(id+"F6.wireOp",EDGE,"E50");
            cPoint(context, id + "F53", {"entities" : qUnion([Q0]), "parameter" : 0.5});
        }
        {
            var Q0;
            Q0=qCreatedBy(id+"F53",VERTEX);
            var Q1;
            Q1=sQuery(id+"F6.wireOp",VERTEX,"E56.end");
            var Q2;
            Q2=sQuery(id+"F4.wireOp",VERTEX,"E21.start");
            cPlane(context, id + "F54", {"entities" : qUnion([Q0, Q1, Q2]), "cplaneType" : CPlaneType.THREE_POINT, "offset" : 25.4 * mm, "width" : 152.4 * mm, "height" : 152.4 * mm});
        }
        {
            var Q0;
            Q0=qCreatedBy(id+"F54.planeOp",FACE);
            var sketch = newSketch(context, id + "F55", { "sketchPlane" : qUnion([Q0])});
            skLineSegment(sketch, "E134.bottom", {"start": v(-51.37, -31.75) * mm, "end": v(-71, -31.75) * mm});
            skLineSegment(sketch, "E134.top", {"start": v(-51.37, 31.75) * mm, "end": v(-71, 31.75) * mm});
            skLineSegment(sketch, "E134.left", {"start": v(-51.37, -31.75) * mm, "end": v(-51.37, 31.75) * mm});
            skLineSegment(sketch, "E134.right", {"start": v(-71, -31.75) * mm, "end": v(-71, 31.75) * mm});
            skLineSegment(sketch, "E135", {"start": v(-51.37, -31.75) * mm, "end": v(-63.5, 31.75) * mm});
            skSolve(sketch);
        }
        {
            var Q0;
            Q0=makeQuery(id+"F55.imprint","IMPRINT",FACE,{"disambiguationData":[TD([[makeQuery(id+"F55.imprint","IMPRINT",EDGE,{"derivedFrom":sQuery(id+"F55.wireOp",EDGE,"E134.bottom")}),-1.0]])]});
            extrude(context, id + "F56", {"entities" : qUnion([Q0]), "operationType" : NewBodyOperationType.REMOVE, "endBound" : BoundingType.THROUGH_ALL, "oppositeDirection" : true, "depth" : 25.4 * mm, "offsetDistance" : 25.4 * mm, "hasSecondDirection" : true, "secondDirectionBound" : SecondDirectionBoundingType.THROUGH_ALL, "secondDirectionOppositeDirection" : false, "secondDirectionDepth" : 25.4 * mm});
        }
        {
            var Q0;
            Q0=sQuery(id+"F6.wireOp",VERTEX,"E49.end");
            var Q1;
            Q1=sQuery(id+"F4.wireOp",VERTEX,"E26.start");
            var Q2;
            Q2=sQuery(id+"F4.wireOp",VERTEX,"E26.end");
            cPlane(context, id + "F57", {"entities" : qUnion([Q0, Q1, Q2]), "cplaneType" : CPlaneType.THREE_POINT, "offset" : 25.4 * mm, "width" : 152.4 * mm, "height" : 152.4 * mm});
        }
        {
            var Q0;
            Q0=qCreatedBy(id+"F57.planeOp",FACE);
            var sketch = newSketch(context, id + "F58", { "sketchPlane" : qUnion([Q0])});
            skLineSegment(sketch, "E136.bottom", {"start": v(51.37, 31.75) * mm, "end": v(71, 31.75) * mm});
            skLineSegment(sketch, "E136.top", {"start": v(51.37, -31.75) * mm, "end": v(71, -31.75) * mm});
            skLineSegment(sketch, "E136.left", {"start": v(51.37, 31.75) * mm, "end": v(51.37, -31.75) * mm});
            skLineSegment(sketch, "E136.right", {"start": v(71, 31.75) * mm, "end": v(71, -31.75) * mm});
            skLineSegment(sketch, "E137", {"start": v(51.37, 31.75) * mm, "end": v(63.5, -31.75) * mm});
            skSolve(sketch);
        }
        {
            var Q0;
            Q0=makeQuery(id+"F58.imprint","IMPRINT",FACE,{"disambiguationData":[TD([[makeQuery(id+"F58.imprint","IMPRINT",EDGE,{"derivedFrom":sQuery(id+"F58.wireOp",EDGE,"E136.bottom")}),-1.0]])]});
            extrude(context, id + "F59", {"entities" : qUnion([Q0]), "operationType" : NewBodyOperationType.REMOVE, "endBound" : BoundingType.THROUGH_ALL, "oppositeDirection" : true, "depth" : 25.4 * mm, "offsetDistance" : 25.4 * mm, "hasSecondDirection" : true, "secondDirectionBound" : SecondDirectionBoundingType.THROUGH_ALL, "secondDirectionOppositeDirection" : false, "secondDirectionDepth" : 25.4 * mm});
        }
        {
            var Q0;
            Q0=sQuery(id+"F4.wireOp",VERTEX,"E41.start");
            var Q1;
            Q1=sQuery(id+"F7.wireOp",VERTEX,"E75.end");
            var Q2;
            Q2=sQuery(id+"F4.wireOp",VERTEX,"E38.start");
            cPlane(context, id + "F60", {"entities" : qUnion([Q0, Q1, Q2]), "cplaneType" : CPlaneType.THREE_POINT, "offset" : 25.4 * mm, "width" : 152.4 * mm, "height" : 152.4 * mm});
        }
        {
            var Q0;
            Q0=qCreatedBy(id+"F60.planeOp",FACE);
            var sketch = newSketch(context, id + "F61", { "sketchPlane" : qUnion([Q0])});
            skLineSegment(sketch, "E138", {"start": v(0, 71) * mm, "end": v(51.37, 31.75) * mm});
            skLineSegment(sketch, "E139", {"start": v(0, 71) * mm, "end": v(63.5, 71) * mm});
            skLineSegment(sketch, "E140", {"start": v(63.5, 71) * mm, "end": v(63.5, 31.75) * mm});
            skLineSegment(sketch, "E141", {"start": v(63.5, 31.75) * mm, "end": v(51.37, 31.75) * mm});
            skSolve(sketch);
        }
        {
            var Q0;
            {var subQ0=sQuery(id+"F61.wireOp",EDGE,"E138");Q0=makeQuery(id+"F61.imprint","IMPRINT",FACE,{"disambiguationData":[TD([[makeQuery(id+"F61.imprint","IMPRINT",EDGE,{"derivedFrom":subQ0}),1.0]])]});}
            var Q1;
            Q1=sQuery(id+"F4.wireOp",VERTEX,"E21.end");
            var Q2;
            Q2=sQuery(id+"F4.wireOp",VERTEX,"E22.end");
            extrude(context, id + "F62", {"entities" : qUnion([Q0]), "operationType" : NewBodyOperationType.REMOVE, "endBound" : BoundingType.UP_TO_VERTEX, "depth" : 25.4 * mm, "endBoundEntityVertex" : qUnion([Q1]), "offsetDistance" : 25.4 * mm, "hasSecondDirection" : true, "secondDirectionBound" : SecondDirectionBoundingType.UP_TO_VERTEX, "secondDirectionOppositeDirection" : true, "secondDirectionDepth" : 25.4 * mm, "secondDirectionBoundEntityVertex" : qUnion([Q2])});
        }
        {
            var Q0;
            Q0=sQuery(id+"F7.wireOp",VERTEX,"E75.end");
            var Q1;
            Q1=sQuery(id+"F4.wireOp",VERTEX,"E41.start");
            var Q2;
            Q2=sQuery(id+"F4.wireOp",VERTEX,"E26.end");
            cPlane(context, id + "F63", {"entities" : qUnion([Q0, Q1, Q2]), "cplaneType" : CPlaneType.THREE_POINT, "offset" : 25.4 * mm, "width" : 152.4 * mm, "height" : 152.4 * mm});
        }
        {
            var Q0;
            Q0=qCreatedBy(id+"F63.planeOp",FACE);
            var sketch = newSketch(context, id + "F64", { "sketchPlane" : qUnion([Q0])});
            skLineSegment(sketch, "E142", {"start": v(0, 71) * mm, "end": v(-51.37, 31.75) * mm});
            skLineSegment(sketch, "E143", {"start": v(0, 71) * mm, "end": v(-63.5, 71) * mm});
            skLineSegment(sketch, "E144", {"start": v(-63.5, 71) * mm, "end": v(-63.5, 31.75) * mm});
            skLineSegment(sketch, "E145", {"start": v(-63.5, 31.75) * mm, "end": v(-51.37, 31.75) * mm});
            skSolve(sketch);
        }
        {
            var Q0;
            Q0=makeQuery(id+"F64.imprint","IMPRINT",FACE,{"disambiguationData":[TD([[makeQuery(id+"F64.imprint","IMPRINT",EDGE,{"derivedFrom":sQuery(id+"F64.wireOp",EDGE,"E142")}),-1.0]])]});
            extrude(context, id + "F65", {"entities" : qUnion([Q0]), "operationType" : NewBodyOperationType.REMOVE, "endBound" : BoundingType.THROUGH_ALL, "oppositeDirection" : true, "depth" : 25.4 * mm, "offsetDistance" : 25.4 * mm, "hasSecondDirection" : true, "secondDirectionBound" : SecondDirectionBoundingType.THROUGH_ALL, "secondDirectionOppositeDirection" : false, "secondDirectionDepth" : 25.4 * mm});
        }
        {
            var Q0;
            Q0=sQuery(id+"F7.wireOp",VERTEX,"E75.end");
            var Q1;
            Q1=sQuery(id+"F4.wireOp",VERTEX,"E41.start");
            var Q2;
            Q2=sQuery(id+"F4.wireOp",VERTEX,"E33.end");
            cPlane(context, id + "F66", {"entities" : qUnion([Q0, Q1, Q2]), "cplaneType" : CPlaneType.THREE_POINT, "offset" : 25.4 * mm, "width" : 152.4 * mm, "height" : 152.4 * mm});
        }
        {
            var Q0;
            Q0=qCreatedBy(id+"F66.planeOp",FACE);
            var sketch = newSketch(context, id + "F67", { "sketchPlane" : qUnion([Q0])});
            skLineSegment(sketch, "E146", {"start": v(0, 71) * mm, "end": v(-51.37, 31.75) * mm});
            skLineSegment(sketch, "E147", {"start": v(0, 71) * mm, "end": v(-63.5, 71) * mm});
            skLineSegment(sketch, "E148", {"start": v(-63.5, 71) * mm, "end": v(-63.5, 31.75) * mm});
            skLineSegment(sketch, "E149", {"start": v(-63.5, 31.75) * mm, "end": v(-51.37, 31.75) * mm});
            skSolve(sketch);
        }
        {
            var Q0;
            {var subQ0=sQuery(id+"F67.wireOp",EDGE,"E146");Q0=makeQuery(id+"F67.imprint","IMPRINT",FACE,{"disambiguationData":[TD([[makeQuery(id+"F67.imprint","IMPRINT",EDGE,{"derivedFrom":subQ0}),-1.0]])]});}
            extrude(context, id + "F68", {"entities" : qUnion([Q0]), "operationType" : NewBodyOperationType.REMOVE, "endBound" : BoundingType.THROUGH_ALL, "oppositeDirection" : true, "depth" : 25.4 * mm, "offsetDistance" : 25.4 * mm, "hasSecondDirection" : true, "secondDirectionBound" : SecondDirectionBoundingType.THROUGH_ALL, "secondDirectionOppositeDirection" : false, "secondDirectionDepth" : 25.4 * mm});
        }
        {
            var Q0;
            Q0=sQuery(id+"F4.wireOp",VERTEX,"E30.end");
            var Q1;
            Q1=sQuery(id+"F4.wireOp",VERTEX,"E41.start");
            var Q2;
            Q2=sQuery(id+"F7.wireOp",VERTEX,"E75.end");
            cPlane(context, id + "F69", {"entities" : qUnion([Q0, Q1, Q2]), "cplaneType" : CPlaneType.THREE_POINT, "offset" : 25.4 * mm, "width" : 152.4 * mm, "height" : 152.4 * mm});
        }
        {
            var Q0;
            Q0=qCreatedBy(id+"F69.planeOp",FACE);
            var sketch = newSketch(context, id + "F70", { "sketchPlane" : qUnion([Q0])});
            skLineSegment(sketch, "E150", {"start": v(0, 71) * mm, "end": v(51.37, 31.75) * mm});
            skLineSegment(sketch, "E151", {"start": v(0, 71) * mm, "end": v(63.5, 71) * mm});
            skLineSegment(sketch, "E152", {"start": v(63.5, 71) * mm, "end": v(63.5, 31.75) * mm});
            skLineSegment(sketch, "E153", {"start": v(63.5, 31.75) * mm, "end": v(51.37, 31.75) * mm});
            skSolve(sketch);
        }
        {
            var Q0;
            Q0=makeQuery(id+"F70.imprint","IMPRINT",FACE,{"disambiguationData":[TD([[makeQuery(id+"F70.imprint","IMPRINT",EDGE,{"derivedFrom":sQuery(id+"F70.wireOp",EDGE,"E150")}),1.0]])]});
            extrude(context, id + "F71", {"entities" : qUnion([Q0]), "operationType" : NewBodyOperationType.REMOVE, "endBound" : BoundingType.THROUGH_ALL, "oppositeDirection" : true, "depth" : 25.4 * mm, "offsetDistance" : 25.4 * mm, "hasSecondDirection" : true, "secondDirectionBound" : SecondDirectionBoundingType.THROUGH_ALL, "secondDirectionOppositeDirection" : false, "secondDirectionDepth" : 25.4 * mm});
        }
        {
            var Q0;
            Q0=sQuery(id+"F4.wireOp",VERTEX,"E27.end");
            var Q1;
            Q1=sQuery(id+"F4.wireOp",VERTEX,"E41.start");
            var Q2;
            Q2=sQuery(id+"F7.wireOp",VERTEX,"E75.end");
            cPlane(context, id + "F72", {"entities" : qUnion([Q0, Q1, Q2]), "cplaneType" : CPlaneType.THREE_POINT, "offset" : 25.4 * mm, "width" : 152.4 * mm, "height" : 152.4 * mm});
        }
        {
            var Q0;
            Q0=qCreatedBy(id+"F72.planeOp",FACE);
            var sketch = newSketch(context, id + "F73", { "sketchPlane" : qUnion([Q0])});
            skLineSegment(sketch, "E154", {"start": v(0, 71) * mm, "end": v(51.37, 31.75) * mm});
            skLineSegment(sketch, "E155", {"start": v(0, 71) * mm, "end": v(63.5, 71) * mm});
            skLineSegment(sketch, "E156", {"start": v(63.5, 71) * mm, "end": v(63.5, 31.75) * mm});
            skLineSegment(sketch, "E157", {"start": v(63.5, 31.75) * mm, "end": v(51.37, 31.75) * mm});
            skSolve(sketch);
        }
        {
            var Q0;
            {var subQ0=sQuery(id+"F73.wireOp",EDGE,"E154");Q0=makeQuery(id+"F73.imprint","IMPRINT",FACE,{"disambiguationData":[TD([[makeQuery(id+"F73.imprint","IMPRINT",EDGE,{"derivedFrom":subQ0}),1.0]])]});}
            extrude(context, id + "F74", {"entities" : qUnion([Q0]), "operationType" : NewBodyOperationType.REMOVE, "endBound" : BoundingType.THROUGH_ALL, "oppositeDirection" : true, "depth" : 25.4 * mm, "offsetDistance" : 25.4 * mm, "hasSecondDirection" : true, "secondDirectionBound" : SecondDirectionBoundingType.THROUGH_ALL, "secondDirectionOppositeDirection" : false, "secondDirectionDepth" : 25.4 * mm});
        }
        {
            var Q0;
            Q0=makeQuery(id+"F65.boolean.opBoolean","COPY",FACE,{"derivedFrom":makeQuery(id+"F65.opExtrude","SWEPT_FACE",FACE,{"disambiguationData":[OSD([sQuery(id+"F64.wireOp",EDGE,"E142")])]})});
            var sketch = newSketch(context, id + "F75", { "sketchPlane" : qUnion([Q0])});
            skText(sketch, "E158", { "text": "1", "fontName": "OpenSans-Bold.ttf"});
            skLineSegment(sketch, "E159", {"start": v(-37.32, -21.55) * mm, "end": v(0, 43.1) * mm});
            skLineSegment(sketch, "E160", {"start": v(0, 43.1) * mm, "end": v(37.32, -21.55) * mm});
            skLineSegment(sketch, "E161", {"start": v(37.32, -21.55) * mm, "end": v(-37.32, -21.55) * mm});
            skLineSegment(sketch, "E162.0", {"start": v(0, 30.4) * mm, "end": v(26.33, -15.2) * mm});
            skLineSegment(sketch, "E162.1", {"start": v(-26.33, -15.2) * mm, "end": v(0, 30.4) * mm});
            skLineSegment(sketch, "E162.2", {"start": v(26.33, -15.2) * mm, "end": v(-26.33, -15.2) * mm});
            const initialGuessF75  = {"E158": [-0.01221, -0.01159, 1, 0, 0.02712]};
            skSetInitialGuess(sketch, initialGuessF75);
            skSolve(sketch);
        }
        {
            var Q0;
            Q0=makeQuery(id+"F75.imprint","IMPRINT",FACE,{"disambiguationData":[TD([[makeQuery(id+"F75.imprint","IMPRINT",EDGE,{"derivedFrom":sQuery(id+"F75.wireOp",EDGE,"E158.sketch_text.stroke-0")}),1.0]])]});
            extrude(context, id + "F76", {"entities" : qUnion([Q0]), "operationType" : NewBodyOperationType.REMOVE, "oppositeDirection" : true, "depth" : 2.54 * mm, "offsetDistance" : 25.4 * mm});
        }
        {
            var Q0;
            Q0=makeQuery(id+"F21.boolean.opBoolean","COPY",FACE,{"derivedFrom":makeQuery(id+"F21.opExtrude","SWEPT_FACE",FACE,{"disambiguationData":[OSD([sQuery(id+"F20.wireOp",EDGE,"E110")])]})});
            var sketch = newSketch(context, id + "F77", { "sketchPlane" : qUnion([Q0])});
            skLineSegment(sketch, "E163", {"start": v(0, 43.1) * mm, "end": v(37.32, -21.55) * mm});
            skLineSegment(sketch, "E164", {"start": v(37.32, -21.55) * mm, "end": v(-37.32, -21.55) * mm});
            skLineSegment(sketch, "E165", {"start": v(-37.32, -21.55) * mm, "end": v(0, 43.1) * mm});
            skLineSegment(sketch, "E166.0", {"start": v(0, 30.4) * mm, "end": v(26.33, -15.2) * mm});
            skLineSegment(sketch, "E166.1", {"start": v(-26.33, -15.2) * mm, "end": v(0, 30.4) * mm});
            skLineSegment(sketch, "E166.2", {"start": v(26.33, -15.2) * mm, "end": v(-26.33, -15.2) * mm});
            skText(sketch, "E167", { "text": "20\n", "fontName": "OpenSans-Bold.ttf"});
            const initialGuessF77  = {"E167": [-0.01524, -0.00785, 1, 0, 0.01874]};
            skSetInitialGuess(sketch, initialGuessF77);
            skSolve(sketch);
        }
        {
            var Q0;
            {var subQ8=sQuery(id+"F77.wireOp",EDGE,"E166.0");Q0=makeQuery(id+"F77.imprint","IMPRINT",FACE,{"disambiguationData":[TD([[makeQuery(id+"F77.imprint","IMPRINT",EDGE,{"derivedFrom":subQ8}),-1.0]])]});}
            var Q1;
            Q1=makeQuery(id+"F77.imprint","IMPRINT",FACE,{"disambiguationData":[TD([[makeQuery(id+"F77.imprint","IMPRINT",EDGE,{"derivedFrom":sQuery(id+"F77.wireOp",EDGE,"E167.sketch_text.stroke-32")}),1.0]])]});
            extrude(context, id + "F78", {"entities" : qUnion([Q0, Q1]), "operationType" : NewBodyOperationType.REMOVE, "oppositeDirection" : true, "depth" : 2.54 * mm, "offsetDistance" : 25.4 * mm});
        }
    });
